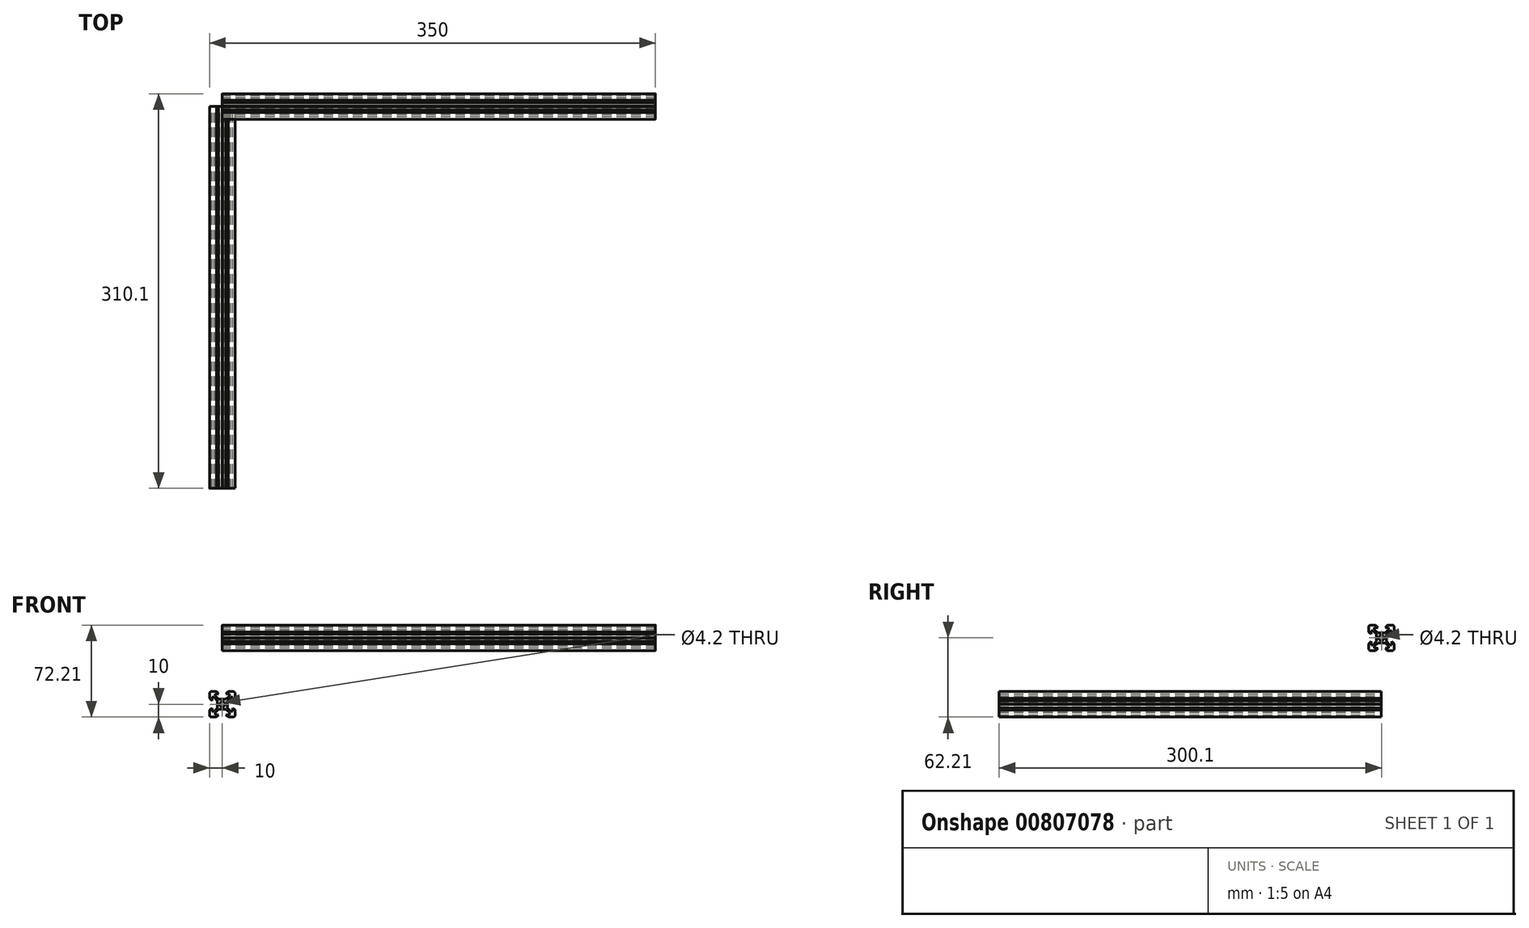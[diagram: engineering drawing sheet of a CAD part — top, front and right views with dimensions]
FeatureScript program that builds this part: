
annotation { "Feature Type Name" : "Feature", "Feature Type Description" : "" }
export const myFeature = defineFeature(function(context is Context, id is Id, definition is map)
    precondition{}
    {
        {
            var Q0;
            Q0=qCreatedBy(makeId("Front.planeOp"),FACE);
            var sketch = newSketch(context, id + "F0", { "sketchPlane" : qUnion([Q0])});
            skArc(sketch, "E0", {"start": v(-8.5, 10) * mm, "mid": v(-9.56, 9.56) * mm, "end": v(-10, 8.5) * mm});
            skLineSegment(sketch, "E1", {"start": v(-10, 8.5) * mm, "end": v(-10, 4.64) * mm});
            skLineSegment(sketch, "E2", {"start": v(-10, 4.64) * mm, "end": v(-8.2, 2.84) * mm});
            skLineSegment(sketch, "E3", {"start": v(-8.2, 5.5) * mm, "end": v(-8.2, 2.84) * mm});
            skLineSegment(sketch, "E4", {"start": v(-8.2, 5.5) * mm, "end": v(-6.56, 5.5) * mm});
            skLineSegment(sketch, "E5", {"start": v(-6.56, 5.5) * mm, "end": v(-3.9, 2.84) * mm});
            skLineSegment(sketch, "E6", {"start": v(-3.9, 2.84) * mm, "end": v(-3.9, 0.2) * mm});
            skLineSegment(sketch, "E7", {"start": v(-3.9, 0.2) * mm, "end": v(-3.7, 0) * mm});
            skLineSegment(sketch, "E8", {"start": v(-3.9, -0.2) * mm, "end": v(-3.7, 0) * mm});
            skLineSegment(sketch, "E9", {"start": v(-3.9, -2.84) * mm, "end": v(-3.9, -0.2) * mm});
            skLineSegment(sketch, "E10", {"start": v(-6.56, -5.5) * mm, "end": v(-3.9, -2.84) * mm});
            skLineSegment(sketch, "E11", {"start": v(-8.2, -5.5) * mm, "end": v(-6.56, -5.5) * mm});
            skLineSegment(sketch, "E12", {"start": v(-8.2, -5.5) * mm, "end": v(-8.2, -2.84) * mm});
            skLineSegment(sketch, "E13", {"start": v(-10, -4.64) * mm, "end": v(-8.2, -2.84) * mm});
            skLineSegment(sketch, "E14", {"start": v(-10, -8.5) * mm, "end": v(-10, -4.64) * mm});
            skArc(sketch, "E15", {"start": v(-10, -8.5) * mm, "mid": v(-9.56, -9.56) * mm, "end": v(-8.5, -10) * mm});
            skLineSegment(sketch, "E16", {"start": v(-8.5, -10) * mm, "end": v(-4.64, -10) * mm});
            skLineSegment(sketch, "E17", {"start": v(-4.64, -10) * mm, "end": v(-2.84, -8.2) * mm});
            skLineSegment(sketch, "E18", {"start": v(-2.84, -8.2) * mm, "end": v(-5.5, -8.2) * mm});
            skLineSegment(sketch, "E19", {"start": v(-5.5, -8.2) * mm, "end": v(-5.5, -6.56) * mm});
            skLineSegment(sketch, "E20", {"start": v(-5.5, -6.56) * mm, "end": v(-2.84, -3.9) * mm});
            skLineSegment(sketch, "E21", {"start": v(-0.2, -3.9) * mm, "end": v(-2.84, -3.9) * mm});
            skLineSegment(sketch, "E22", {"start": v(-0.2, -3.9) * mm, "end": v(0, -3.7) * mm});
            skLineSegment(sketch, "E23", {"start": v(0.2, -3.9) * mm, "end": v(0, -3.7) * mm});
            skLineSegment(sketch, "E24", {"start": v(0.2, -3.9) * mm, "end": v(2.84, -3.9) * mm});
            skLineSegment(sketch, "E25", {"start": v(5.5, -6.56) * mm, "end": v(2.84, -3.9) * mm});
            skLineSegment(sketch, "E26", {"start": v(5.5, -8.2) * mm, "end": v(5.5, -6.56) * mm});
            skLineSegment(sketch, "E27", {"start": v(2.84, -8.2) * mm, "end": v(5.5, -8.2) * mm});
            skLineSegment(sketch, "E28", {"start": v(4.64, -10) * mm, "end": v(2.84, -8.2) * mm});
            skLineSegment(sketch, "E29", {"start": v(8.5, -10) * mm, "end": v(4.64, -10) * mm});
            skArc(sketch, "E30", {"start": v(8.5, -10) * mm, "mid": v(9.56, -9.56) * mm, "end": v(10, -8.5) * mm});
            skLineSegment(sketch, "E31", {"start": v(10, -8.5) * mm, "end": v(10, -4.64) * mm});
            skLineSegment(sketch, "E32", {"start": v(10, -4.64) * mm, "end": v(8.2, -2.84) * mm});
            skLineSegment(sketch, "E33", {"start": v(8.2, -5.5) * mm, "end": v(8.2, -2.84) * mm});
            skLineSegment(sketch, "E34", {"start": v(8.2, -5.5) * mm, "end": v(6.56, -5.5) * mm});
            skLineSegment(sketch, "E35", {"start": v(6.56, -5.5) * mm, "end": v(3.9, -2.84) * mm});
            skLineSegment(sketch, "E36", {"start": v(3.9, -2.84) * mm, "end": v(3.9, -0.2) * mm});
            skLineSegment(sketch, "E37", {"start": v(3.9, -0.2) * mm, "end": v(3.7, 0) * mm});
            skLineSegment(sketch, "E38", {"start": v(3.9, 0.2) * mm, "end": v(3.7, 0) * mm});
            skLineSegment(sketch, "E39", {"start": v(3.9, 2.84) * mm, "end": v(3.9, 0.2) * mm});
            skLineSegment(sketch, "E40", {"start": v(6.56, 5.5) * mm, "end": v(3.9, 2.84) * mm});
            skLineSegment(sketch, "E41", {"start": v(8.2, 5.5) * mm, "end": v(6.56, 5.5) * mm});
            skLineSegment(sketch, "E42", {"start": v(8.2, 5.5) * mm, "end": v(8.2, 2.84) * mm});
            skLineSegment(sketch, "E43", {"start": v(10, 4.64) * mm, "end": v(8.2, 2.84) * mm});
            skLineSegment(sketch, "E44", {"start": v(10, 8.5) * mm, "end": v(10, 4.64) * mm});
            skArc(sketch, "E45", {"start": v(10, 8.5) * mm, "mid": v(9.56, 9.56) * mm, "end": v(8.5, 10) * mm});
            skLineSegment(sketch, "E46", {"start": v(8.5, 10) * mm, "end": v(4.64, 10) * mm});
            skLineSegment(sketch, "E47", {"start": v(4.64, 10) * mm, "end": v(2.84, 8.2) * mm});
            skLineSegment(sketch, "E48", {"start": v(2.84, 8.2) * mm, "end": v(5.5, 8.2) * mm});
            skLineSegment(sketch, "E49", {"start": v(5.5, 8.2) * mm, "end": v(5.5, 6.56) * mm});
            skLineSegment(sketch, "E50", {"start": v(5.5, 6.56) * mm, "end": v(2.84, 3.9) * mm});
            skLineSegment(sketch, "E51", {"start": v(0.2, 3.9) * mm, "end": v(2.84, 3.9) * mm});
            skLineSegment(sketch, "E52", {"start": v(0.2, 3.9) * mm, "end": v(0, 3.7) * mm});
            skLineSegment(sketch, "E53", {"start": v(-0.2, 3.9) * mm, "end": v(0, 3.7) * mm});
            skLineSegment(sketch, "E54", {"start": v(-0.2, 3.9) * mm, "end": v(-2.84, 3.9) * mm});
            skLineSegment(sketch, "E55", {"start": v(-5.5, 6.56) * mm, "end": v(-2.84, 3.9) * mm});
            skLineSegment(sketch, "E56", {"start": v(-5.5, 8.2) * mm, "end": v(-5.5, 6.56) * mm});
            skLineSegment(sketch, "E57", {"start": v(-2.84, 8.2) * mm, "end": v(-5.5, 8.2) * mm});
            skLineSegment(sketch, "E58", {"start": v(-4.64, 10) * mm, "end": v(-2.84, 8.2) * mm});
            skLineSegment(sketch, "E59", {"start": v(-8.5, 10) * mm, "end": v(-4.64, 10) * mm});
            skCircle(sketch, "E60", {"center": v(0, 0) * mm, "radius": 2.1 * mm});
            skSolve(sketch);
        }
        {
            var Q0;
            Q0=qCreatedBy(makeId("Right.planeOp"),FACE);
            var sketch = newSketch(context, id + "F1", { "sketchPlane" : qUnion([Q0])});
            skArc(sketch, "E61", {"start": v(-8.4, 62.2) * mm, "mid": v(-9.46, 61.77) * mm, "end": v(-9.9, 60.7) * mm});
            skLineSegment(sketch, "E62", {"start": v(-9.9, 60.7) * mm, "end": v(-9.9, 56.85) * mm});
            skLineSegment(sketch, "E63", {"start": v(-9.9, 56.85) * mm, "end": v(-8.1, 55.05) * mm});
            skLineSegment(sketch, "E64", {"start": v(-8.1, 57.7) * mm, "end": v(-8.1, 55.05) * mm});
            skLineSegment(sketch, "E65", {"start": v(-8.1, 57.7) * mm, "end": v(-6.46, 57.7) * mm});
            skLineSegment(sketch, "E66", {"start": v(-6.46, 57.7) * mm, "end": v(-3.8, 55.05) * mm});
            skLineSegment(sketch, "E67", {"start": v(-3.8, 55.05) * mm, "end": v(-3.8, 52.4) * mm});
            skLineSegment(sketch, "E68", {"start": v(-3.8, 52.4) * mm, "end": v(-3.6, 52.2) * mm});
            skLineSegment(sketch, "E69", {"start": v(-3.8, 52) * mm, "end": v(-3.6, 52.2) * mm});
            skLineSegment(sketch, "E70", {"start": v(-3.8, 49.37) * mm, "end": v(-3.8, 52) * mm});
            skLineSegment(sketch, "E71", {"start": v(-6.46, 46.71) * mm, "end": v(-3.8, 49.37) * mm});
            skLineSegment(sketch, "E72", {"start": v(-8.1, 46.71) * mm, "end": v(-6.46, 46.71) * mm});
            skLineSegment(sketch, "E73", {"start": v(-8.1, 46.71) * mm, "end": v(-8.1, 49.37) * mm});
            skLineSegment(sketch, "E74", {"start": v(-9.9, 47.57) * mm, "end": v(-8.1, 49.37) * mm});
            skLineSegment(sketch, "E75", {"start": v(-9.9, 43.7) * mm, "end": v(-9.9, 47.57) * mm});
            skArc(sketch, "E76", {"start": v(-9.9, 43.7) * mm, "mid": v(-9.46, 42.65) * mm, "end": v(-8.4, 42.2) * mm});
            skLineSegment(sketch, "E77", {"start": v(-8.4, 42.2) * mm, "end": v(-4.54, 42.2) * mm});
            skLineSegment(sketch, "E78", {"start": v(-4.54, 42.2) * mm, "end": v(-2.74, 44) * mm});
            skLineSegment(sketch, "E79", {"start": v(-2.74, 44) * mm, "end": v(-5.4, 44) * mm});
            skLineSegment(sketch, "E80", {"start": v(-5.4, 44) * mm, "end": v(-5.4, 45.65) * mm});
            skLineSegment(sketch, "E81", {"start": v(-5.4, 45.65) * mm, "end": v(-2.74, 48.3) * mm});
            skLineSegment(sketch, "E82", {"start": v(-0.1, 48.3) * mm, "end": v(-2.74, 48.3) * mm});
            skLineSegment(sketch, "E83", {"start": v(-0.1, 48.3) * mm, "end": v(0.1, 48.5) * mm});
            skLineSegment(sketch, "E84", {"start": v(0.3, 48.3) * mm, "end": v(0.1, 48.5) * mm});
            skLineSegment(sketch, "E85", {"start": v(0.3, 48.3) * mm, "end": v(2.94, 48.3) * mm});
            skLineSegment(sketch, "E86", {"start": v(5.6, 45.65) * mm, "end": v(2.94, 48.3) * mm});
            skLineSegment(sketch, "E87", {"start": v(5.6, 44) * mm, "end": v(5.6, 45.65) * mm});
            skLineSegment(sketch, "E88", {"start": v(2.94, 44) * mm, "end": v(5.6, 44) * mm});
            skLineSegment(sketch, "E89", {"start": v(4.74, 42.2) * mm, "end": v(2.94, 44) * mm});
            skLineSegment(sketch, "E90", {"start": v(8.6, 42.2) * mm, "end": v(4.74, 42.2) * mm});
            skArc(sketch, "E91", {"start": v(8.6, 42.2) * mm, "mid": v(9.66, 42.65) * mm, "end": v(10.1, 43.7) * mm});
            skLineSegment(sketch, "E92", {"start": v(10.1, 43.7) * mm, "end": v(10.1, 47.57) * mm});
            skLineSegment(sketch, "E93", {"start": v(10.1, 47.57) * mm, "end": v(8.3, 49.37) * mm});
            skLineSegment(sketch, "E94", {"start": v(8.3, 46.71) * mm, "end": v(8.3, 49.37) * mm});
            skLineSegment(sketch, "E95", {"start": v(8.3, 46.71) * mm, "end": v(6.66, 46.71) * mm});
            skLineSegment(sketch, "E96", {"start": v(6.66, 46.71) * mm, "end": v(4, 49.37) * mm});
            skLineSegment(sketch, "E97", {"start": v(4, 49.37) * mm, "end": v(4, 52) * mm});
            skLineSegment(sketch, "E98", {"start": v(4, 52) * mm, "end": v(3.8, 52.2) * mm});
            skLineSegment(sketch, "E99", {"start": v(4, 52.4) * mm, "end": v(3.8, 52.2) * mm});
            skLineSegment(sketch, "E100", {"start": v(4, 55.05) * mm, "end": v(4, 52.4) * mm});
            skLineSegment(sketch, "E101", {"start": v(6.66, 57.7) * mm, "end": v(4, 55.05) * mm});
            skLineSegment(sketch, "E102", {"start": v(8.3, 57.7) * mm, "end": v(6.66, 57.7) * mm});
            skLineSegment(sketch, "E103", {"start": v(8.3, 57.7) * mm, "end": v(8.3, 55.05) * mm});
            skLineSegment(sketch, "E104", {"start": v(10.1, 56.85) * mm, "end": v(8.3, 55.05) * mm});
            skLineSegment(sketch, "E105", {"start": v(10.1, 60.7) * mm, "end": v(10.1, 56.85) * mm});
            skArc(sketch, "E106", {"start": v(10.1, 60.7) * mm, "mid": v(9.66, 61.77) * mm, "end": v(8.6, 62.2) * mm});
            skLineSegment(sketch, "E107", {"start": v(8.6, 62.2) * mm, "end": v(4.74, 62.2) * mm});
            skLineSegment(sketch, "E108", {"start": v(4.74, 62.2) * mm, "end": v(2.94, 60.4) * mm});
            skLineSegment(sketch, "E109", {"start": v(2.94, 60.4) * mm, "end": v(5.6, 60.4) * mm});
            skLineSegment(sketch, "E110", {"start": v(5.6, 60.4) * mm, "end": v(5.6, 58.77) * mm});
            skLineSegment(sketch, "E111", {"start": v(5.6, 58.77) * mm, "end": v(2.94, 56.11) * mm});
            skLineSegment(sketch, "E112", {"start": v(0.3, 56.11) * mm, "end": v(2.94, 56.11) * mm});
            skLineSegment(sketch, "E113", {"start": v(0.3, 56.11) * mm, "end": v(0.1, 55.91) * mm});
            skLineSegment(sketch, "E114", {"start": v(-0.1, 56.11) * mm, "end": v(0.1, 55.91) * mm});
            skLineSegment(sketch, "E115", {"start": v(-0.1, 56.11) * mm, "end": v(-2.74, 56.11) * mm});
            skLineSegment(sketch, "E116", {"start": v(-5.4, 58.77) * mm, "end": v(-2.74, 56.11) * mm});
            skLineSegment(sketch, "E117", {"start": v(-5.4, 60.4) * mm, "end": v(-5.4, 58.77) * mm});
            skLineSegment(sketch, "E118", {"start": v(-2.74, 60.4) * mm, "end": v(-5.4, 60.4) * mm});
            skLineSegment(sketch, "E119", {"start": v(-4.54, 62.2) * mm, "end": v(-2.74, 60.4) * mm});
            skLineSegment(sketch, "E120", {"start": v(-8.4, 62.2) * mm, "end": v(-4.54, 62.2) * mm});
            skCircle(sketch, "E121", {"center": v(0.1, 52.2) * mm, "radius": 2.1 * mm});
            skSolve(sketch);
        }
        {
            var Q0;
            Q0=makeQuery(id+"F0.imprint","IMPRINT",FACE,{"disambiguationData":[TD([[makeQuery(id+"F0.imprint","IMPRINT",EDGE,{"derivedFrom":sQuery(id+"F0.wireOp",EDGE,"E0")}),1.0]])]});
            extrude(context, id + "F2", {"entities" : qUnion([Q0]), "depth" : 300 * mm, "offsetDistance" : 25 * mm});
        }
        {
            var Q0;
            Q0=makeQuery(id+"F1.imprint","IMPRINT",FACE,{"disambiguationData":[TD([[makeQuery(id+"F1.imprint","IMPRINT",EDGE,{"derivedFrom":sQuery(id+"F1.wireOp",EDGE,"E61")}),1.0]])]});
            extrude(context, id + "F3", {"entities" : qUnion([Q0]), "depth" : 340 * mm, "offsetDistance" : 25 * mm});
        }
    });
